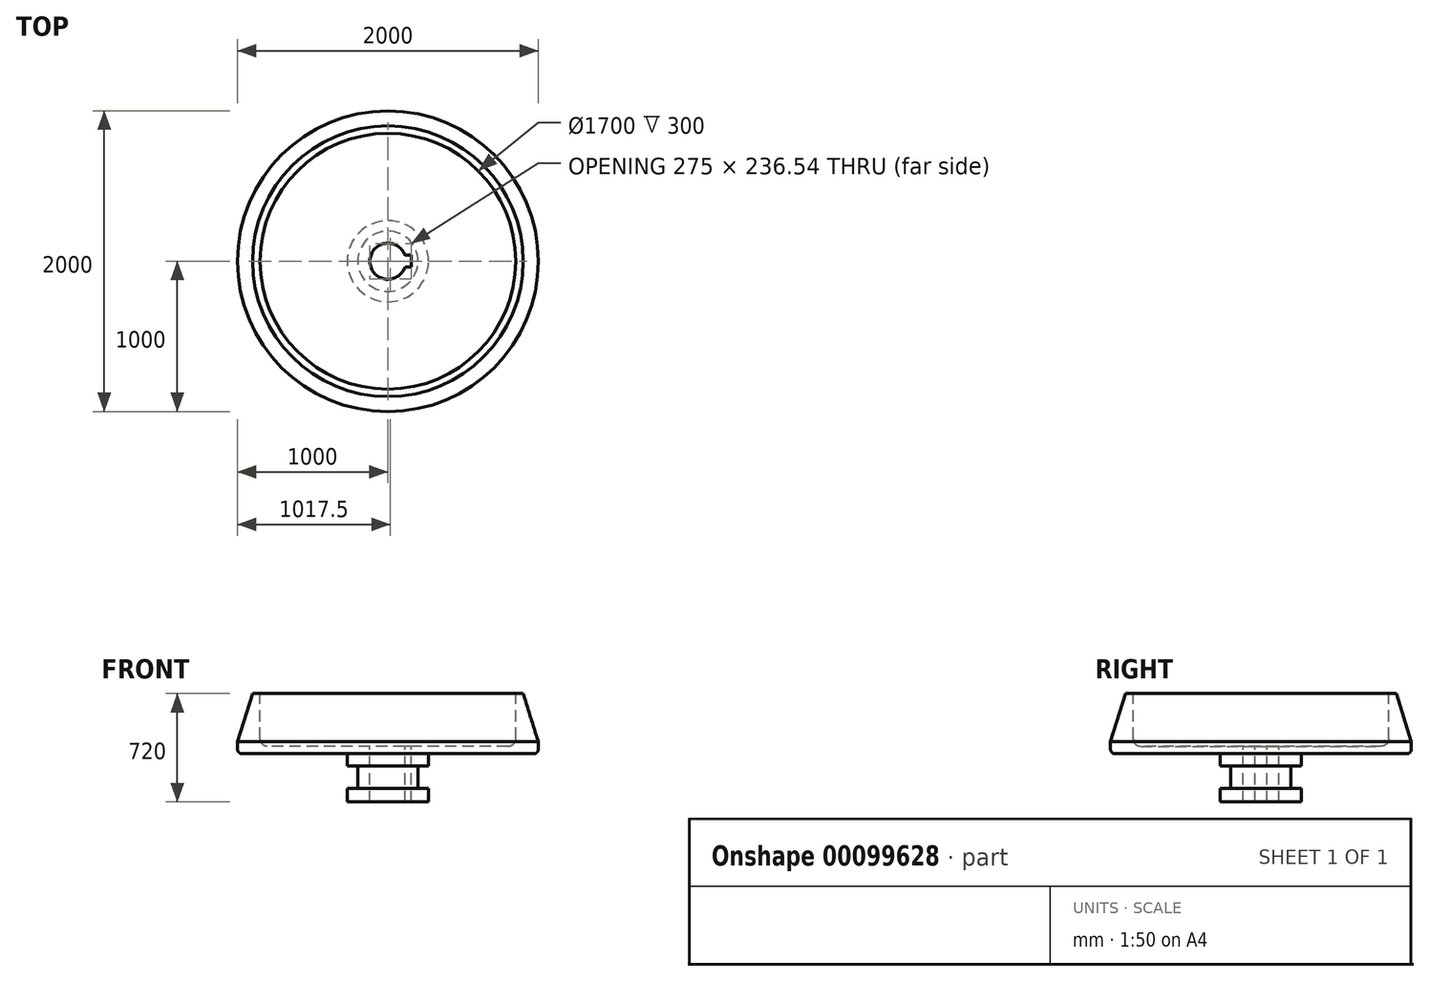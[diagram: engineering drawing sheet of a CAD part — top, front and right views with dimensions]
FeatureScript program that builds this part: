
annotation { "Feature Type Name" : "Feature", "Feature Type Description" : "" }
export const myFeature = defineFeature(function(context is Context, id is Id, definition is map)
    precondition{}
    {
        {
            var Q0;
            Q0=qCreatedBy(makeId("Front.planeOp"),FACE);
            var sketch = newSketch(context, id + "F0", { "sketchPlane" : qUnion([Q0])});
            skLineSegment(sketch, "E0", {"start": v(0, -423.95) * mm, "end": v(270, -423.95) * mm});
            skLineSegment(sketch, "E1", {"start": v(270, -423.95) * mm, "end": v(270, -333.95) * mm});
            skLineSegment(sketch, "E2", {"start": v(270, -333.95) * mm, "end": v(200, -333.95) * mm});
            skLineSegment(sketch, "E3", {"start": v(200, -333.95) * mm, "end": v(200, -183.95) * mm});
            skLineSegment(sketch, "E4", {"start": v(200, -183.95) * mm, "end": v(270, -183.95) * mm});
            skLineSegment(sketch, "E5", {"start": v(270, -183.95) * mm, "end": v(270, -103.95) * mm});
            skLineSegment(sketch, "E6", {"start": v(270, -103.95) * mm, "end": v(970, -103.95) * mm});
            skLineSegment(sketch, "E7", {"start": v(1000, -73.95) * mm, "end": v(1000, -23.95) * mm});
            skLineSegment(sketch, "E8", {"start": v(850, 296.05) * mm, "end": v(850, -3.95) * mm});
            skLineSegment(sketch, "E9", {"start": v(800, -53.95) * mm, "end": v(0, -53.95) * mm});
            skLineSegment(sketch, "E10", {"start": v(0, -53.95) * mm, "end": v(0, -423.95) * mm});
            skLineSegment(sketch, "E11", {"start": v(850, 296.05) * mm, "end": v(900, 296.05) * mm});
            skLineSegment(sketch, "E12", {"start": v(900, 296.05) * mm, "end": v(1000, -23.95) * mm});
            skPoint(sketch, "E13.visualSharp", {"position": v(850, -53.95) * mm});
            skArc(sketch, "E13.filletArc", {"start": v(800, -53.95) * mm, "mid": v(835.36, -39.3) * mm, "end": v(850, -3.95) * mm});
            skPoint(sketch, "E14.visualSharp", {"position": v(1000, -103.95) * mm});
            skArc(sketch, "E14.filletArc", {"start": v(970, -103.95) * mm, "mid": v(991.21, -95.16) * mm, "end": v(1000, -73.95) * mm});
            skSolve(sketch);
        }
        {
            var Q0;
            Q0 = qSketchRegion(id + "F0", true);
            var Q1;
            Q1=sQuery(id+"F0.wireOp",EDGE,"E10");
            revolve(context, id + "F1", {"entities" : qUnion([Q0]), "axis" : qUnion([Q1]), "revolveType" : RevolveType.FULL});
        }
        {
            var Q0;
            Q0=makeQuery(id+"F1.opRevolve","SWEPT_FACE",FACE,{"disambiguationData":[OSD([sQuery(id+"F0.wireOp",EDGE,"E9")])]});
            var sketch = newSketch(context, id + "F2", { "sketchPlane" : qUnion([Q0])});
            skArc(sketch, "E15", {"start": v(113.14, 40) * mm, "mid": v(-120, 0) * mm, "end": v(113.14, -40) * mm});
            skLineSegment(sketch, "E16.bottom", {"start": v(155, -40) * mm, "end": v(113.14, -40) * mm});
            skLineSegment(sketch, "E16.top", {"start": v(155, 40) * mm, "end": v(113.14, 40) * mm});
            skLineSegment(sketch, "E16.left", {"start": v(155, -40) * mm, "end": v(155, 40) * mm});
            skPoint(sketch, "E16.middle", {"position": v(120, 0) * mm});
            skPoint(sketch, "E16.right.end.orphan", {"position": v(85, 40) * mm});
            skPoint(sketch, "E17.orphan", {"position": v(85, -40) * mm});
            skSolve(sketch);
        }
        {
            var Q0;
            Q0 = qSketchRegion(id + "F2", true);
            extrude(context, id + "F3", {"entities" : qUnion([Q0]), "operationType" : NewBodyOperationType.REMOVE, "endBound" : BoundingType.THROUGH_ALL, "oppositeDirection" : true, "depth" : 25 * mm});
        }
    });
